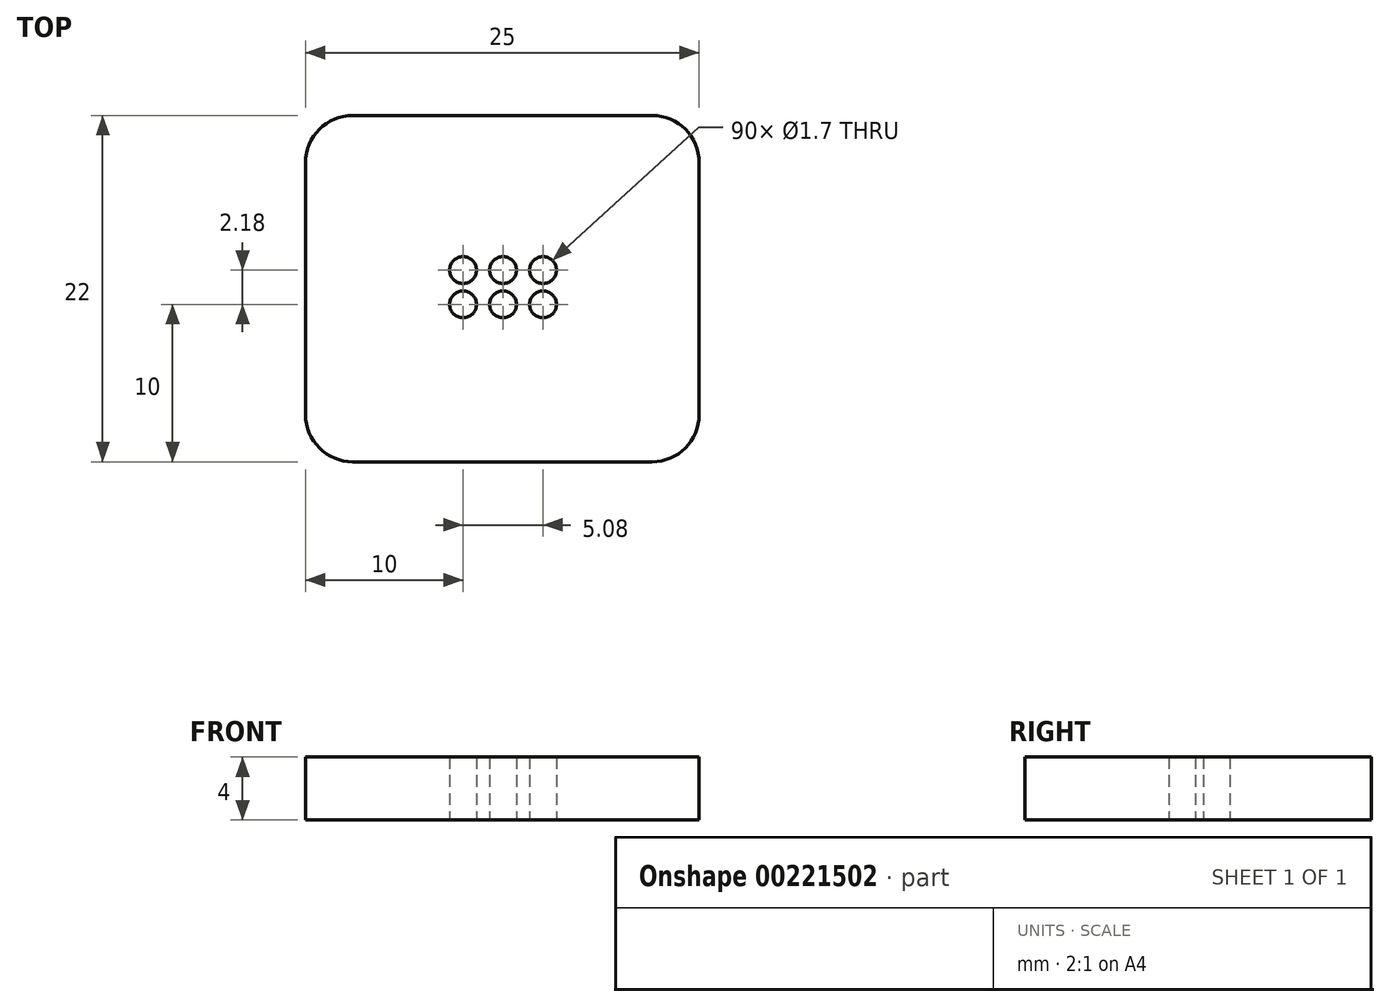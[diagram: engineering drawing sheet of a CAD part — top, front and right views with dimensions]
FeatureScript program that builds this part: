
annotation { "Feature Type Name" : "Feature", "Feature Type Description" : "" }
export const myFeature = defineFeature(function(context is Context, id is Id, definition is map)
    precondition{}
    {
        {
            var Q0;
            Q0=qCreatedBy(makeId("Top.planeOp"),FACE);
            var sketch = newSketch(context, id + "F0", { "sketchPlane" : qUnion([Q0])});
            skLineSegment(sketch, "E0.bottom", {"start": v(3, 0) * mm, "end": v(22, 0) * mm});
            skLineSegment(sketch, "E0.top", {"start": v(3, 22) * mm, "end": v(22, 22) * mm});
            skLineSegment(sketch, "E0.left", {"start": v(0, 3) * mm, "end": v(0, 19) * mm});
            skLineSegment(sketch, "E0.right", {"start": v(25, 3) * mm, "end": v(25, 19) * mm});
            skPoint(sketch, "E1.visualSharp", {"position": v(25, 22) * mm});
            skArc(sketch, "E1.filletArc", {"start": v(25, 19) * mm, "mid": v(24.12, 21.12) * mm, "end": v(22, 22) * mm});
            skPoint(sketch, "E2.visualSharp", {"position": v(0, 22) * mm});
            skArc(sketch, "E2.filletArc", {"start": v(3, 22) * mm, "mid": v(0.88, 21.12) * mm, "end": v(0, 19) * mm});
            skPoint(sketch, "E3.visualSharp", {"position": v(0, 0) * mm});
            skArc(sketch, "E3.filletArc", {"start": v(0, 3) * mm, "mid": v(0.88, 0.88) * mm, "end": v(3, 0) * mm});
            skPoint(sketch, "E4.visualSharp", {"position": v(25, 0) * mm});
            skArc(sketch, "E4.filletArc", {"start": v(22, 0) * mm, "mid": v(24.12, 0.88) * mm, "end": v(25, 3) * mm});
            skCircle(sketch, "E5", {"center": v(10, 10) * mm, "radius": 0.85 * mm});
            skCircle(sketch, "E6.1.0.0", {"center": v(10, 12.18) * mm, "radius": 0.85 * mm});
            skLineSegment(sketch, "E6.direction1", {"start": v(10, 10) * mm, "end": v(10, 12.18) * mm, "construction": true});
            skCircle(sketch, "E7.1.0.0", {"center": v(12.54, 12.18) * mm, "radius": 0.85 * mm});
            skCircle(sketch, "E7.1.0.1", {"center": v(12.54, 10) * mm, "radius": 0.85 * mm});
            skCircle(sketch, "E7.2.0.0", {"center": v(15.08, 12.18) * mm, "radius": 0.85 * mm});
            skCircle(sketch, "E7.2.0.1", {"center": v(15.08, 10) * mm, "radius": 0.85 * mm});
            skLineSegment(sketch, "E7.direction1", {"start": v(10, 10) * mm, "end": v(12.54, 10) * mm, "construction": true});
            skSolve(sketch);
        }
        {
            var Q0;
            Q0=makeQuery(id+"F0.imprint","IMPRINT",FACE,{"disambiguationData":[TD([[makeQuery(id+"F0.imprint","IMPRINT",EDGE,{"derivedFrom":sQuery(id+"F0.wireOp",EDGE,"E0.bottom")}),1.0]])]});
            extrude(context, id + "F1", {"entities" : qUnion([Q0]), "depth" : 4 * mm});
        }
    });
